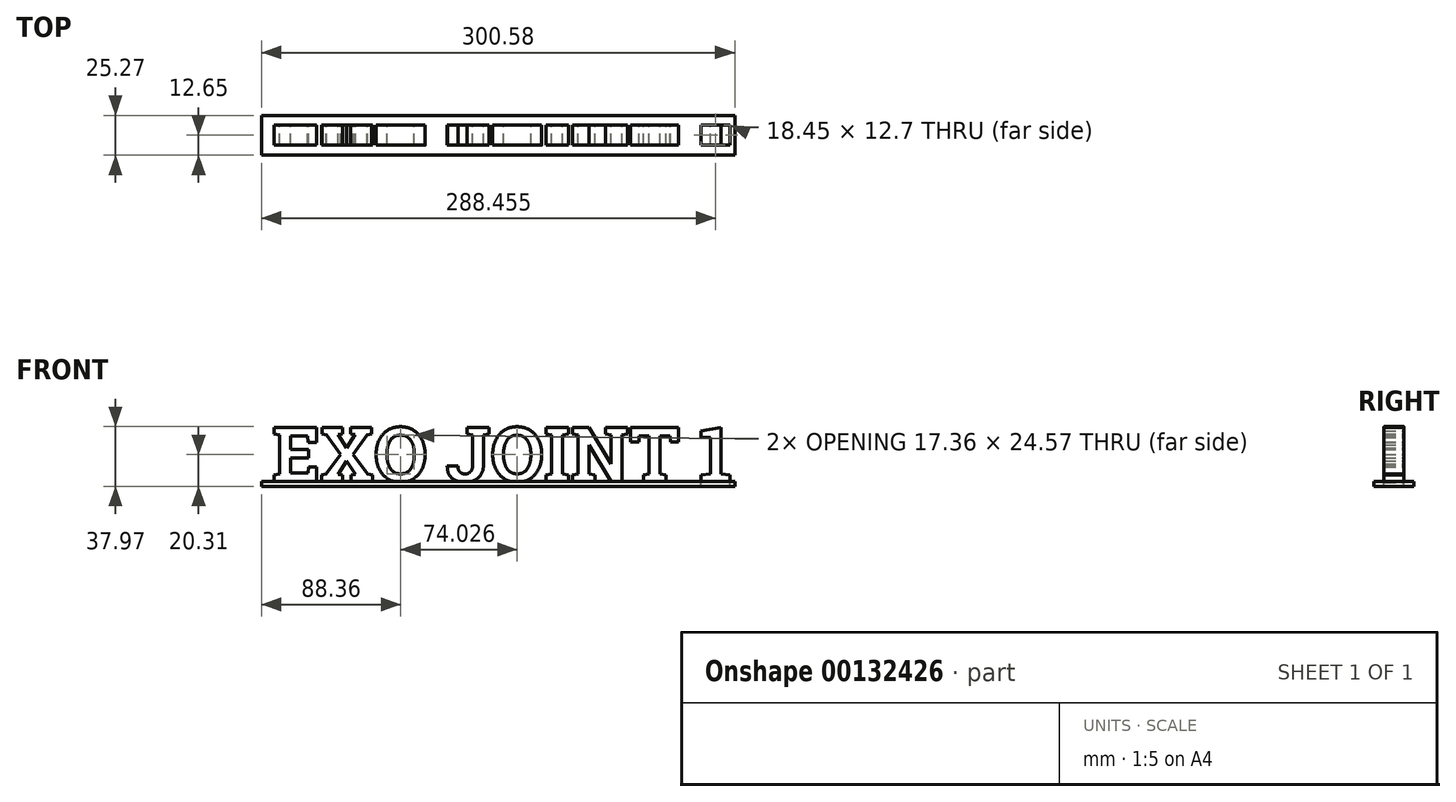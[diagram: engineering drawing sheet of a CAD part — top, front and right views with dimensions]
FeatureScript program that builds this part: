
annotation { "Feature Type Name" : "Feature", "Feature Type Description" : "" }
export const myFeature = defineFeature(function(context is Context, id is Id, definition is map)
    precondition{}
    {
        {
            var Q0;
            Q0=qCreatedBy(makeId("Front.planeOp"),FACE);
            var sketch = newSketch(context, id + "F0", { "sketchPlane" : qUnion([Q0])});
            skText(sketch, "E0", { "text": "EXO JOINT 1", "fontName": "RobotoSlab-Bold.ttf"});
            const initialGuessF0  = {"E0": [-0.14832, -0.01562, 1, 0, 0.03474]};
            skSetInitialGuess(sketch, initialGuessF0);
            skSolve(sketch);
        }
        {
            var Q0;
            Q0 = qSketchRegion(id + "F0", true);
            extrude(context, id + "F1", {"entities" : qUnion([Q0]), "depth" : 12.7 * mm});
        }
        {
            var Q0;
            Q0=makeQuery(id+"F1.opExtrude","SWEPT_FACE",FACE,{"disambiguationData":[OSD([sQuery(id+"F0.wireOp",EDGE,"E0.sketch_text.stroke-167")])]});
            var sketch = newSketch(context, id + "F2", { "sketchPlane" : qUnion([Q0])});
            skLineSegment(sketch, "E1.bottom", {"start": v(-154.84, 19) * mm, "end": v(145.74, 19) * mm});
            skLineSegment(sketch, "E1.top", {"start": v(-154.84, -6.27) * mm, "end": v(145.74, -6.27) * mm});
            skLineSegment(sketch, "E1.left", {"start": v(-154.84, 19) * mm, "end": v(-154.84, -6.27) * mm});
            skLineSegment(sketch, "E1.right", {"start": v(145.74, 19) * mm, "end": v(145.74, -6.27) * mm});
            skSolve(sketch);
        }
        {
            var Q0;
            Q0=makeQuery(id+"F2.imprint","IMPRINT",FACE,{"disambiguationData":[TD([[makeQuery(id+"F2.imprint","IMPRINT",EDGE,{"derivedFrom":sQuery(id+"F2.wireOp",EDGE,"E1.bottom")}),-1.0]])]});
            extrude(context, id + "F3", {"entities" : qUnion([Q0]), "depth" : 3.17 * mm});
        }
    });
